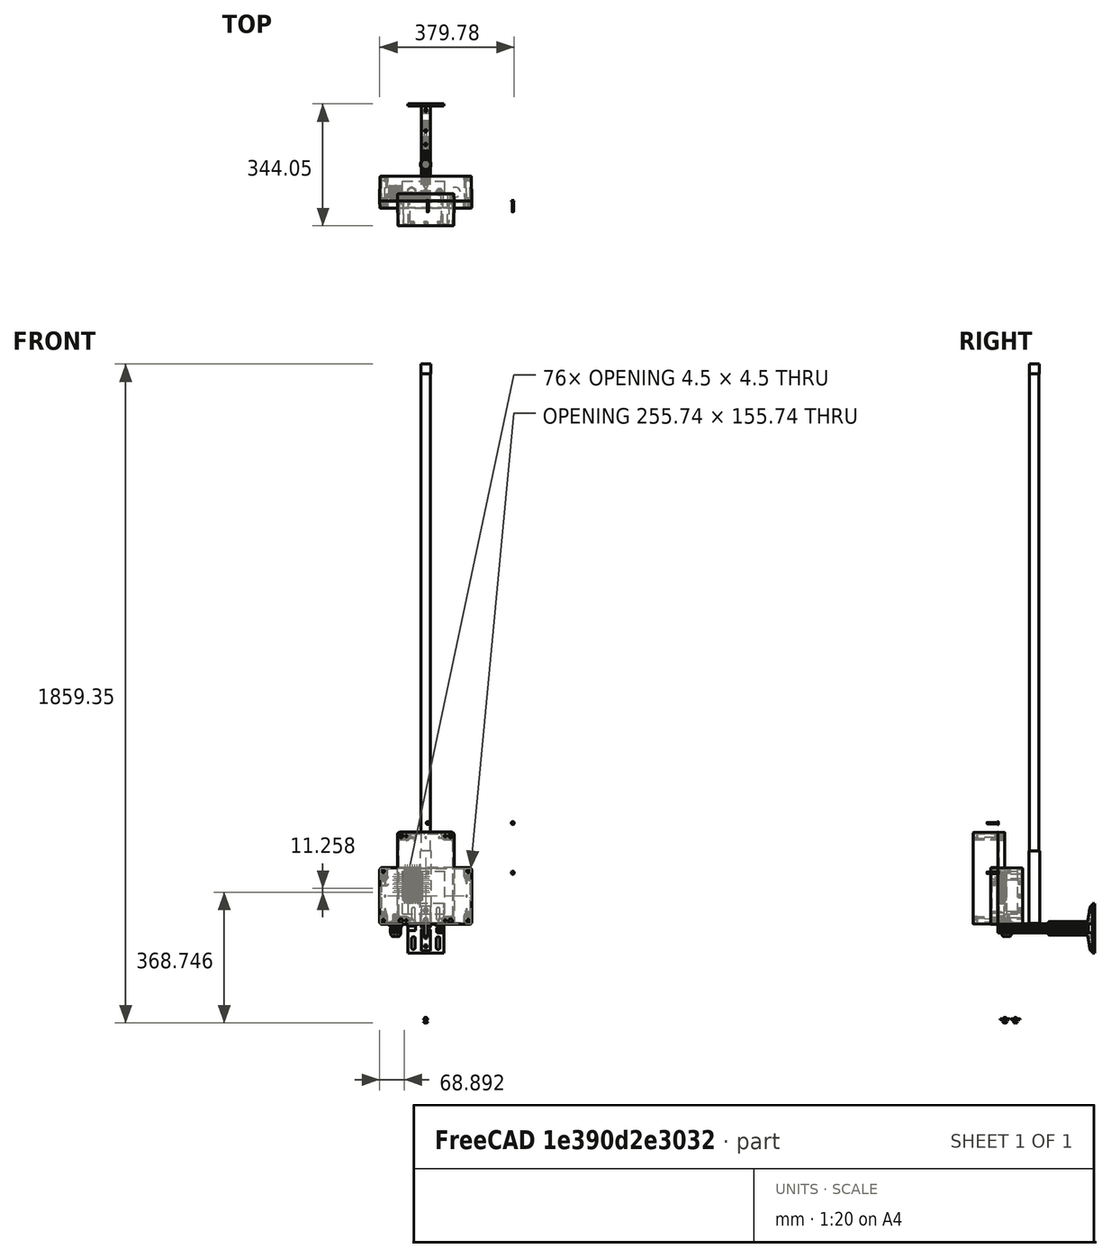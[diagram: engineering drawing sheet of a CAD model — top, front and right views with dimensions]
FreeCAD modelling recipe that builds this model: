
FCSTD DOCUMENT  (FreeCAD 0.20R29410 (Git))
Label: gateWayModule
License: All rights reserved
LicenseURL: http://en.wikipedia.org/wiki/All_rights_reserved
objects: Part::Feature×42, TechDraw::DrawViewDimension×36, Part::Cylinder×28, Part::MultiFuse×9, App::Part×8, Part::Cut×4, TechDraw::DrawViewPart×4, TechDraw::DrawSVGTemplate×2, TechDraw::DrawPage×2, Part::Box×1, Sketcher::SketchObject×1, Part::Extrusion×1, TechDraw::DrawViewAnnotation×1
note: 86 computed .brp shape members not serialized (recipe doc carries the construction recipe); baked Part::Feature solids carry a one-line shape summary decoded from their .brp

FEATURE [Part::Feature] Part__Feature  label="AN-23B_AN-23BP-01"
  shape: bbox 160 x 71.5 x 260 mm, 302 faces (baked)
FEATURE [Part::Feature] Part__Feature001  label="AN-23C_AN-23C-01"
  shape: bbox 160.5 x 20 x 260.5 mm, 243 faces (baked)
FEATURE [Part::Feature] Part__Feature002  label="cross recessed countersunk head screw_jis_JIS 1111 Cross recessed countersunk head screw - M4 x 32 - Z --24CSST"
  Placement = pos=(245.578,1.4369,155.7) rot=(0.642635,-0.642635,0.417181;3.93205rad)
  shape: bbox 8.4 x 32 x 8.4 mm, 32 faces (baked)
FEATURE [Part::Feature] Part__Feature003  label="cross recessed countersunk head screw_jis_JIS 1111 Cross recessed countersunk head screw - M4 x 32 - Z --24CSST001"
  Placement = pos=(245.578,1.4369,15.6996) rot=(0.610522,-0.610522,0.504506;4.07608rad)
  shape: bbox 8.4 x 32 x 8.4 mm, 32 faces (baked)
FEATURE [Part::Feature] Part__Feature004  label="cross recessed countersunk head screw_jis_JIS 1111 Cross recessed countersunk head screw - M4 x 32 - Z --24CSST002"
  Placement = pos=(5.5776,1.4369,15.6996) rot=(0.641113,-0.641113,0.421839;3.93997rad)
  shape: bbox 8.4 x 32 x 8.4 mm, 32 faces (baked)
FEATURE [Part::Feature] Part__Feature005  label="cross recessed countersunk head screw_jis_JIS 1111 Cross recessed countersunk head screw - M4 x 32 - Z --24CSST003"
  Placement = pos=(5.5776,1.4369,155.7) rot=(0.666667,-0.666667,0.333333;3.78509rad)
  shape: bbox 8.4 x 32 x 8.4 mm, 32 faces (baked)
FEATURE [App::Part] SCREWS_036_4  label="SCREWS-036-4"
  Group = -> [Part__Feature002,Part__Feature003,Part__Feature004,Part__Feature005]
  Origin = -> Origin
  Placement = pos=(85.6996,18.1356,-125.578) rot=(0,-1,0;1.5708rad)
FEATURE [Part::Feature] Part__Feature006  label="GASKET-123-01"
  Placement = pos=(0,1.04,0) rot=(0,0,1;0rad)
  shape: bbox 157.7 x 1.5 x 257.7 mm, 98 faces (baked)
FEATURE [App::Part] AN_23P_01  label="AN-23P-01"
  Group = -> [Part__Feature,Part__Feature001,SCREWS_036_4,Part__Feature006]
  Origin = -> Origin001
  Placement = pos=(0,0,-50) rot=(0.707107,0,-0.707107;3.14159rad)
FEATURE [Part::Box] Box  label="Gateway"
  AttacherType = Attacher::AttachEngine3D
  Height = 120
  Length = 120
  Placement = pos=(-66,26,-100) rot=(0,0,1;0rad)
  Width = 30
FEATURE [Part::Cylinder] Cylinder030  label="loraAntenna"
  Angle = 360
  AttacherType = Attacher::AttachEngine3D
  FirstAngle = 0
  Height = 1390
  Radius = 13
  SecondAngle = 0
FEATURE [Part::Cylinder] Cylinder031  label="loraAntenna001"
  Angle = 360
  AttacherType = Attacher::AttachEngine3D
  FirstAngle = 0
  Height = 204
  Radius = 15
  SecondAngle = 0
FEATURE [Part::Cylinder] Cylinder032  label="loraAntenna002"
  Angle = 360
  AttacherType = Attacher::AttachEngine3D
  FirstAngle = 0
  Height = 27
  Placement = pos=(0,0,1363) rot=(0,0,1;0rad)
  Radius = 14
  SecondAngle = 0
FEATURE [Part::MultiFuse] Fusion006  label="loraAntenna003"
  Placement = pos=(0,0,188) rot=(0,0,1;0rad)
  Shapes = -> [Cylinder030,Cylinder032]
FEATURE [Part::MultiFuse] Fusion007  label="loraAntenna004"
  Placement = pos=(0,103,-127) rot=(0,0,1;0rad)
  Shapes = -> [Fusion006,Cylinder031]
FEATURE [Part::Feature] Part__Feature008  label="CUI_VGS-25W-5"
  Placement = pos=(-42,23,-27) rot=(1,0,0;3.14159rad)
  shape: bbox 55.36 x 25.53 x 90.37 mm, 2734 faces, 26 solids (baked)
FEATURE [Part::Feature] Part__Feature009  label="DCC-RJ6ST-310"
  Placement = pos=(-85,25,-123) rot=(0,0,1;0rad)
  shape: bbox 40.36 x 68.07 x 51.72 mm, 441 faces (baked)
FEATURE [Part::Feature] Part__Feature010  label="DCP-RJ6ST-F"
  Placement = pos=(-85,25,-123.5) rot=(0,1,0;3.14159rad)
  shape: bbox 40.26 x 40.33 x 38.85 mm, 485 faces, 2 solids (baked)
FEATURE [Part::Cylinder] Cylinder  label="plugIn"
  Angle = 360
  AttacherType = Attacher::AttachEngine3D
  FirstAngle = 0
  Height = 28.19
  Radius = 11
  SecondAngle = 0
FEATURE [Sketcher::SketchObject] Sketch
  FullyConstrained = true
  sketch-geometry (7):
    g0: LineSegment StartX=12.25 StartY=-7.07254 StartZ=0 EndX=12.25 EndY=7.07254 EndZ=0
    g1: LineSegment StartX=12.25 StartY=7.07254 StartZ=0 EndX=0 EndY=14.1451 EndZ=0
    g2: LineSegment StartX=0 StartY=14.1451 StartZ=0 EndX=-12.25 EndY=7.07254 EndZ=0
    g3: LineSegment StartX=-12.25 StartY=7.07254 StartZ=0 EndX=-12.25 EndY=-7.07254 EndZ=0
    g4: LineSegment StartX=-12.25 StartY=-7.07254 StartZ=0 EndX=0 EndY=-14.1451 EndZ=0
    g5: LineSegment StartX=0 StartY=-14.1451 StartZ=0 EndX=12.25 EndY=-7.07254 EndZ=0
    g6: Circle CenterX=0 CenterY=0 CenterZ=0 NormalX=0 NormalY=0 NormalZ=1 AngleXU=0 Radius=14.1451
  constraints (17):
    c: Coincident(g0,g1)
    c: Coincident(g1,g2)
    c: Coincident(g2,g3)
    c: Coincident(g3,g4)
    c: Coincident(g4,g5)
    c: Coincident(g5,g0)
    c: Equal(g0, g1-g5) x5
    c: PointOnObject(g0,g6)
    c: PointOnObject(g1,g6)
    c: PointOnObject(g2,g6)
    c: PointOnObject(g3,g6)
    c: PointOnObject(g4,g6)
    c: PointOnObject(g5,g6)
    c: DistanceY(g6) = 0
    c: DistanceX(g6) = 0
    c: DistanceX(g1) = 0
    c: DistanceX(g2,g0) = 24.5
FEATURE [Part::Extrusion] Extrude
  Base = -> Sketch
  Dir = (0,0,1)
  DirMode = 2
  FaceMakerClass = Part::FaceMakerBullseye
  LengthFwd = 4.83
  LengthRev = 0
  Placement = pos=(0,0,12.19) rot=(0,0,1;0rad)
  Solid = true
  Symmetric = false
FEATURE [Part::MultiFuse] Fusion  label="powerPlug"
  Placement = pos=(-40,25,-147) rot=(0,0,1;0rad)
  Shapes = -> [Cylinder,Extrude]
FEATURE [Part::Feature] Part__Feature021  label="LoRaAntennaGland"
  Placement = pos=(84,25,-120) rot=(-1,0,0;1.5708rad)
  shape: bbox 36.99 x 36.69 x 48.04 mm, 518 faces, 0 solids (baked)
FEATURE [Part::Feature] Part__Feature022  label="3136N138_T-Slotted Framing"
  Placement = pos=(0,200.3,0) rot=(0,0,1;0rad)
  shape: bbox 101.6 x 133.4 x 139.7 mm, 136 faces (baked)
FEATURE [Part::Feature] Part__Feature023  label="47065T801_T-Slotted Framing"
  Placement = pos=(0,288.5,0) rot=(-1,0,0;1.5708rad)
  shape: bbox 25.4 x 152.4 x 25.4 mm, 108 faces (baked)
FEATURE [Part::Feature] Part__Feature024  label="47065T801_T-Slotted Framing001"
  Placement = pos=(0,391.5,0) rot=(-1,0,0;1.5708rad)
  shape: bbox 25.4 x 152.4 x 25.4 mm, 108 faces (baked)
FEATURE [Part::MultiFuse] Fusion008  label="framingSupport"
  Placement = pos=(0,468,-141.41) rot=(0,0,1;3.14159rad)
  Shapes = -> [Part__Feature024,Part__Feature022,Part__Feature023]
FEATURE [Part::Feature] Part__Feature025  label="Cable Gland PG7-PG19 Body_PG008"
  shape: bbox 17.67 x 27.9 x 16 mm, 147 faces (baked)
FEATURE [Part::Feature] Part__Feature026  label="Cable Gland PG7-PG19 Washer_PG008"
  Placement = pos=(0,-2.8,0) rot=(0,0,1;0rad)
  shape: bbox 16.6 x 1.2 x 16.6 mm, 6 faces (baked)
FEATURE [Part::Feature] Part__Feature027  label="Cable Gland PG7-PG19 Lock Nut_PG008"
  Placement = pos=(0,-5.6,0) rot=(0,0,1;3.14159rad)
  shape: bbox 19.6 x 5.77 x 19.6 mm, 32 faces (baked)
FEATURE [Part::Feature] Part__Feature028  label="Cable Gland PG7-PG19 Sleeve_PG008"
  Placement = pos=(0,13.65,0) rot=(0,0,1;0rad)
  shape: bbox 8.4 x 6.7 x 8.4 mm, 6 faces (baked)
FEATURE [Part::Feature] Part__Feature029  label="Cable Gland PG7-PG19 Gland Nut_PG008"
  Placement = pos=(0,10.95,0) rot=(0,-1,0;1.94172rad)
  shape: bbox 16.87 x 14 x 16.87 mm, 64 faces (baked)
FEATURE [Part::MultiFuse] Fusion011  label="pg7-Copper"
  Placement = pos=(39,25,-134) rot=(-1,0,0;1.5708rad)
  Shapes = -> [Part__Feature025,Part__Feature026,Part__Feature027,Part__Feature028,Part__Feature029]
FEATURE [Part::Cylinder] Cylinder033  label="EthernetCut"
  Angle = 360
  AttacherType = Attacher::AttachEngine3D
  FirstAngle = 0
  Height = 50
  Placement = pos=(-85,25,-147) rot=(0,0,1;0rad)
  Radius = 15.1
  SecondAngle = 0
FEATURE [Part::Cylinder] Cylinder034  label="PowerCut"
  Angle = 360
  AttacherType = Attacher::AttachEngine3D
  FirstAngle = 0
  Height = 50
  Placement = pos=(-40,25,-147) rot=(0,0,1;0rad)
  Radius = 11
  SecondAngle = 0
FEATURE [Part::Cylinder] Cylinder035  label="pg7Cut"
  Angle = 360
  AttacherType = Attacher::AttachEngine3D
  FirstAngle = 0
  Height = 50
  Placement = pos=(39,25,-147) rot=(0,0,1;0rad)
  Radius = 6.4
  SecondAngle = 0
FEATURE [Part::Cylinder] Cylinder036  label="AnetnnaCut"
  Angle = 360
  AttacherType = Attacher::AttachEngine3D
  FirstAngle = 0
  Height = 50
  Placement = pos=(84,25,-147) rot=(0,0,1;0rad)
  Radius = 14.2
  SecondAngle = 0
FEATURE [Part::Feature] Part__Feature030  label="47065T139_T-Slotted Framing"
  Placement = pos=(0,20,-405) rot=(0.57735,0.57735,-0.57735;4.18879rad)
  shape: bbox 11.25 x 25.4 x 17.44 mm, 56 faces, 2 solids (baked)
FEATURE [Part::Feature] Part__Feature031  label="47065T139_T-Slotted Framing001"
  Placement = pos=(0,50,-405) rot=(0.57735,0.57735,-0.57735;4.18879rad)
  shape: bbox 11.25 x 25.4 x 17.44 mm, 56 faces, 2 solids (baked)
FEATURE [Part::Cylinder] Cylinder037  label="m5Cut"
  Angle = 360
  AttacherType = Attacher::AttachEngine3D
  FirstAngle = 0
  Height = 50
  Placement = pos=(0,20,-147) rot=(0,0,1;0rad)
  Radius = 3.2
  SecondAngle = 0
FEATURE [Part::Cylinder] Cylinder038  label="m5Cut001"
  Angle = 360
  AttacherType = Attacher::AttachEngine3D
  FirstAngle = 0
  Height = 50
  Placement = pos=(0,50,-147) rot=(0,0,1;0rad)
  Radius = 3.2
  SecondAngle = 0
FEATURE [Part::MultiFuse] Fusion012
  Shapes = -> [Cylinder038,Cylinder037,Cylinder036,Cylinder035,Cylinder033,Cylinder034]
FEATURE [Part::Cut] Cut
  Base = -> AN_23P_01
  Tool = -> Fusion012
FEATURE [TechDraw::DrawSVGTemplate] Template
  EditableTexts = Designed_by_Name=Lakitha Wijeratne; Drawing_number=V1; FC-Date=November 14th 2022; FC-SC=0.5; FC-Title=MINTS Gateway Module; Subtitle=Cutouts for Polycase AN-23P Black
  Height = 210
  Orientation = 1
  Width = 297
FEATURE [TechDraw::DrawViewPart] View  label="Internal View"
  CoarseView = false
  Direction = (0.577,-0.577,0.577)
  Focus = 100
  HardHidden = false
  IsoCount = 0
  IsoHidden = false
  IsoVisible = false
  LockPosition = false
  Perspective = false
  Rotation = 0
  Scale = 0.5
  ScaleType = 0
  SeamHidden = false
  SeamVisible = true
  SmoothHidden = false
  SmoothVisible = true
  Source = -> [Cut]
  X = 221.274
  XDirection = (0.707,0.707,0)
  Y = 135.96
FEATURE [TechDraw::DrawViewPart] View001  label="Bottom View"
  CoarseView = false
  Direction = (0,0,-1)
  Focus = 100
  HardHidden = false
  IsoCount = 0
  IsoHidden = false
  IsoVisible = false
  LockPosition = false
  Perspective = false
  Rotation = 0
  Scale = 0.5
  ScaleType = 0
  SeamHidden = false
  SeamVisible = true
  SmoothHidden = false
  SmoothVisible = true
  Source = -> [Cut]
  X = 84.2092
  XDirection = (1,0,0)
  Y = 168.275
FEATURE [Part::Cylinder] Cylinder039  label="EthernetCut001"
  Angle = 360
  AttacherType = Attacher::AttachEngine3D
  FirstAngle = 0
  Height = 50
  Placement = pos=(-85,25,-147) rot=(0,0,1;0rad)
  Radius = 15.1
  SecondAngle = 0
FEATURE [Part::Cylinder] Cylinder040  label="PowerCut001"
  Angle = 360
  AttacherType = Attacher::AttachEngine3D
  FirstAngle = 0
  Height = 50
  Placement = pos=(-40,25,-147) rot=(0,0,1;0rad)
  Radius = 11
  SecondAngle = 0
FEATURE [Part::Cylinder] Cylinder041  label="pg7Cut001"
  Angle = 360
  AttacherType = Attacher::AttachEngine3D
  FirstAngle = 0
  Height = 50
  Placement = pos=(39,25,-147) rot=(0,0,1;0rad)
  Radius = 6.4
  SecondAngle = 0
FEATURE [Part::Cylinder] Cylinder042  label="AnetnnaCut001"
  Angle = 360
  AttacherType = Attacher::AttachEngine3D
  FirstAngle = 0
  Height = 50
  Placement = pos=(84,25,-147) rot=(0,0,1;0rad)
  Radius = 14.2
  SecondAngle = 0
FEATURE [Part::Cylinder] Cylinder043  label="m5Cut002"
  Angle = 360
  AttacherType = Attacher::AttachEngine3D
  FirstAngle = 0
  Height = 50
  Placement = pos=(0,20,-147) rot=(0,0,1;0rad)
  Radius = 3.2
  SecondAngle = 0
FEATURE [Part::Cylinder] Cylinder044  label="m5Cut003"
  Angle = 360
  AttacherType = Attacher::AttachEngine3D
  FirstAngle = 0
  Height = 50
  Placement = pos=(0,50,-147) rot=(0,0,1;0rad)
  Radius = 3.2
  SecondAngle = 0
FEATURE [Part::MultiFuse] Fusion013
  Shapes = -> [Cylinder044,Cylinder043,Cylinder042,Cylinder041,Cylinder039,Cylinder040]
FEATURE [Part::Feature] Part__Feature032  label="AN-23B_AN-23BP-002"
  shape: bbox 160 x 71.5 x 260 mm, 302 faces (baked)
FEATURE [Part::Feature] Part__Feature033  label="AN-23C_AN-23C-002"
  shape: bbox 160.5 x 20 x 260.5 mm, 243 faces (baked)
FEATURE [Part::Feature] Part__Feature034  label="cross recessed countersunk head screw_jis_JIS 1111 Cross recessed countersunk head screw - M4 x 32 - Z --24CSST004"
  Placement = pos=(245.578,1.4369,155.7) rot=(0.642635,-0.642635,0.417181;3.93205rad)
  shape: bbox 8.4 x 32 x 8.4 mm, 32 faces (baked)
FEATURE [Part::Feature] Part__Feature035  label="cross recessed countersunk head screw_jis_JIS 1111 Cross recessed countersunk head screw - M4 x 32 - Z --24CSST005"
  Placement = pos=(245.578,1.4369,15.6996) rot=(0.610522,-0.610522,0.504506;4.07608rad)
  shape: bbox 8.4 x 32 x 8.4 mm, 32 faces (baked)
FEATURE [Part::Feature] Part__Feature036  label="cross recessed countersunk head screw_jis_JIS 1111 Cross recessed countersunk head screw - M4 x 32 - Z --24CSST006"
  Placement = pos=(5.5776,1.4369,15.6996) rot=(0.641113,-0.641113,0.421839;3.93997rad)
  shape: bbox 8.4 x 32 x 8.4 mm, 32 faces (baked)
FEATURE [Part::Feature] Part__Feature037  label="cross recessed countersunk head screw_jis_JIS 1111 Cross recessed countersunk head screw - M4 x 32 - Z --24CSST007"
  Placement = pos=(5.5776,1.4369,155.7) rot=(0.666667,-0.666667,0.333333;3.78509rad)
  shape: bbox 8.4 x 32 x 8.4 mm, 32 faces (baked)
FEATURE [Part::Feature] Part__Feature038  label="GASKET-123-002"
  Placement = pos=(0,1.04,0) rot=(0,0,1;0rad)
  shape: bbox 157.7 x 1.5 x 257.7 mm, 98 faces (baked)
FEATURE [App::Part] SCREWS_036_005  label="SCREWS-036-005"
  Group = -> [Part__Feature034,Part__Feature035,Part__Feature036,Part__Feature037]
  Origin = -> Origin002
  Placement = pos=(85.6996,18.1356,-125.578) rot=(0,-1,0;1.5708rad)
FEATURE [App::Part] AN_23P_002  label="AN-23P-002"
  Group = -> [Part__Feature032,Part__Feature033,SCREWS_036_005,Part__Feature038]
  Origin = -> Origin003
  Placement = pos=(0,0,-50) rot=(0.707107,0,-0.707107;3.14159rad)
FEATURE [Part::Cut] Cut001  label="totalView"
  Base = -> AN_23P_002
  Tool = -> Fusion013
FEATURE [TechDraw::DrawViewPart] View002  label="External View"
  CoarseView = false
  Direction = (0.673,-0.641,-0.369)
  Focus = 100
  HardHidden = false
  IsoCount = 0
  IsoHidden = false
  IsoVisible = false
  LockPosition = false
  Perspective = false
  Rotation = 0
  Scale = 0.5
  ScaleType = 0
  SeamHidden = false
  SeamVisible = true
  SmoothHidden = false
  SmoothVisible = true
  Source = -> [Cut001]
  X = 86.3288
  XDirection = (0.739,0.594,0.316)
  Y = 76.7663
FEATURE [TechDraw::DrawViewDimension] Dimension
  AngleOverride = false
  Arbitrary = false
  ArbitraryTolerances = false
  EqualTolerance = true
  ExtensionAngle = 0
  FormatSpec = ⌀%.2w
  FormatSpecOverTolerance = %+.2w
  FormatSpecUnderTolerance = %+.2w
  Inverted = false
  LineAngle = 0
  LockPosition = false
  MeasureType = 1
  OverTolerance = 0
  References2D = -> [View001]
  Rotation = 0
  Scale = 0.5
  ScaleType = 0
  TheoreticalExact = false
  Type = 5
  UnderTolerance = 0
  X = -54.3759
  Y = 16.2133
FEATURE [TechDraw::DrawViewDimension] Dimension001
  AngleOverride = false
  Arbitrary = false
  ArbitraryTolerances = false
  EqualTolerance = true
  ExtensionAngle = 0
  FormatSpec = ⌀%.2w
  FormatSpecOverTolerance = %+.2w
  FormatSpecUnderTolerance = %+.2w
  Inverted = false
  LineAngle = 0
  LockPosition = false
  MeasureType = 1
  OverTolerance = 0
  References2D = -> [View001]
  Rotation = 0
  Scale = 0.5
  ScaleType = 0
  TheoreticalExact = false
  Type = 5
  UnderTolerance = 0
  X = -24.7872
  Y = 16.2975
FEATURE [TechDraw::DrawViewDimension] Dimension002
  AngleOverride = false
  Arbitrary = false
  ArbitraryTolerances = false
  EqualTolerance = true
  ExtensionAngle = 0
  FormatSpec = ⌀%.2w
  FormatSpecOverTolerance = %+.2w
  FormatSpecUnderTolerance = %+.2w
  Inverted = false
  LineAngle = 0
  LockPosition = false
  MeasureType = 1
  OverTolerance = 0
  References2D = -> [View001]
  Rotation = 0
  Scale = 0.5
  ScaleType = 0
  TheoreticalExact = false
  Type = 5
  UnderTolerance = 0
  X = 5.16691
  Y = 14.3503
FEATURE [TechDraw::DrawViewDimension] Dimension003
  AngleOverride = false
  Arbitrary = false
  ArbitraryTolerances = false
  EqualTolerance = true
  ExtensionAngle = 0
  FormatSpec = ⌀%.2w
  FormatSpecOverTolerance = %+.2w
  FormatSpecUnderTolerance = %+.2w
  Inverted = false
  LineAngle = 0
  LockPosition = false
  MeasureType = 1
  OverTolerance = 0
  References2D = -> [View001]
  Rotation = 0
  Scale = 0.5
  ScaleType = 0
  TheoreticalExact = false
  Type = 5
  UnderTolerance = 0
  X = 6.79278
  Y = 3.20489
FEATURE [TechDraw::DrawViewDimension] Dimension004
  AngleOverride = false
  Arbitrary = false
  ArbitraryTolerances = false
  EqualTolerance = true
  ExtensionAngle = 0
  FormatSpec = ⌀%.2w
  FormatSpecOverTolerance = %+.2w
  FormatSpecUnderTolerance = %+.2w
  Inverted = false
  LineAngle = 0
  LockPosition = false
  MeasureType = 1
  OverTolerance = 0
  References2D = -> [View001]
  Rotation = 0
  Scale = 0.5
  ScaleType = 0
  TheoreticalExact = false
  Type = 5
  UnderTolerance = 0
  X = 25.1396
  Y = 14.8713
FEATURE [TechDraw::DrawViewDimension] Dimension005
  AngleOverride = false
  Arbitrary = false
  ArbitraryTolerances = false
  EqualTolerance = true
  ExtensionAngle = 0
  FormatSpec = ⌀%.2w
  FormatSpecOverTolerance = %+.2w
  FormatSpecUnderTolerance = %+.2w
  Inverted = false
  LineAngle = 0
  LockPosition = false
  MeasureType = 1
  OverTolerance = 0
  References2D = -> [View001]
  Rotation = 0
  Scale = 0.5
  ScaleType = 0
  TheoreticalExact = false
  Type = 5
  UnderTolerance = 0
  X = 53.9059
  Y = 15.1805
FEATURE [TechDraw::DrawViewDimension] Dimension006
  AngleOverride = false
  Arbitrary = false
  ArbitraryTolerances = false
  EqualTolerance = true
  ExtensionAngle = 0
  FormatSpec = %.2w
  FormatSpecOverTolerance = %+.2w
  FormatSpecUnderTolerance = %+.2w
  Inverted = false
  LineAngle = 0
  LockPosition = false
  MeasureType = 1
  OverTolerance = 0
  References2D = -> [View001]
  Rotation = 0
  Scale = 0.5
  ScaleType = 0
  TheoreticalExact = false
  Type = 1
  UnderTolerance = 0
  X = -53.7744
  Y = -18.6501
FEATURE [TechDraw::DrawViewDimension] Dimension007
  AngleOverride = false
  Arbitrary = false
  ArbitraryTolerances = false
  EqualTolerance = true
  ExtensionAngle = 0
  FormatSpec = %.2w
  FormatSpecOverTolerance = %+.2w
  FormatSpecUnderTolerance = %+.2w
  Inverted = false
  LineAngle = 0
  LockPosition = false
  MeasureType = 1
  OverTolerance = 0
  References2D = -> [View001]
  Rotation = 0
  Scale = 0.5
  ScaleType = 0
  TheoreticalExact = false
  Type = 1
  UnderTolerance = 0
  X = -35.7058
  Y = -24.4298
FEATURE [TechDraw::DrawViewDimension] Dimension009
  AngleOverride = false
  Arbitrary = false
  ArbitraryTolerances = false
  EqualTolerance = true
  ExtensionAngle = 0
  FormatSpec = %.2w
  FormatSpecOverTolerance = %+.2w
  FormatSpecUnderTolerance = %+.2w
  Inverted = false
  LineAngle = 0
  LockPosition = false
  MeasureType = 1
  OverTolerance = 0
  References2D = -> [View001]
  Rotation = 0
  Scale = 0.5
  ScaleType = 0
  TheoreticalExact = false
  Type = 1
  UnderTolerance = 0
  X = -39.2827
  Y = -33.1748
FEATURE [TechDraw::DrawViewDimension] Dimension010
  AngleOverride = false
  Arbitrary = false
  ArbitraryTolerances = false
  EqualTolerance = true
  ExtensionAngle = 0
  FormatSpec = %.2w
  FormatSpecOverTolerance = %+.2w
  FormatSpecUnderTolerance = %+.2w
  Inverted = false
  LineAngle = 0
  LockPosition = false
  MeasureType = 1
  OverTolerance = 0
  References2D = -> [View001]
  Rotation = 0
  Scale = 0.5
  ScaleType = 0
  TheoreticalExact = false
  Type = 1
  UnderTolerance = 0
  X = 47.8554
  Y = -25.9182
FEATURE [TechDraw::DrawViewDimension] Dimension011
  AngleOverride = false
  Arbitrary = false
  ArbitraryTolerances = false
  EqualTolerance = true
  ExtensionAngle = 0
  FormatSpec = %.2w
  FormatSpecOverTolerance = %+.2w
  FormatSpecUnderTolerance = %+.2w
  Inverted = false
  LineAngle = 0
  LockPosition = false
  MeasureType = 1
  OverTolerance = 0
  References2D = -> [View001]
  Rotation = 0
  Scale = 0.5
  ScaleType = 0
  TheoreticalExact = false
  Type = 1
  UnderTolerance = 0
  X = 54.1367
  Y = -18.5094
FEATURE [TechDraw::DrawViewDimension] Dimension012
  AngleOverride = false
  Arbitrary = false
  ArbitraryTolerances = false
  EqualTolerance = true
  ExtensionAngle = 0
  FormatSpec = %.2w
  FormatSpecOverTolerance = %+.2w
  FormatSpecUnderTolerance = %+.2w
  Inverted = false
  LineAngle = 0
  LockPosition = false
  MeasureType = 1
  OverTolerance = 0
  References2D = -> [View001]
  Rotation = 0
  Scale = 0.5
  ScaleType = 0
  TheoreticalExact = false
  Type = 2
  UnderTolerance = 0
  X = -36.989
  Y = 15.3034
FEATURE [TechDraw::DrawViewDimension] Dimension013
  AngleOverride = false
  Arbitrary = false
  ArbitraryTolerances = false
  EqualTolerance = true
  ExtensionAngle = 0
  FormatSpec = %.2w
  FormatSpecOverTolerance = %+.2w
  FormatSpecUnderTolerance = %+.2w
  Inverted = false
  LineAngle = 0
  LockPosition = false
  MeasureType = 1
  OverTolerance = 0
  References2D = -> [View001]
  Rotation = 0
  Scale = 0.5
  ScaleType = 0
  TheoreticalExact = false
  Type = 1
  UnderTolerance = 0
  X = -29.3162
  Y = 29.8128
FEATURE [TechDraw::DrawViewDimension] Dimension014
  AngleOverride = false
  Arbitrary = false
  ArbitraryTolerances = false
  EqualTolerance = true
  ExtensionAngle = 0
  FormatSpec = %.2w
  FormatSpecOverTolerance = %+.2w
  FormatSpecUnderTolerance = %+.2w
  Inverted = false
  LineAngle = 0
  LockPosition = false
  MeasureType = 1
  OverTolerance = 0
  References2D = -> [View001]
  Rotation = 0
  Scale = 0.5
  ScaleType = 0
  TheoreticalExact = false
  Type = 2
  UnderTolerance = 0
  X = 14.9293
  Y = 13.6113
FEATURE [TechDraw::DrawViewDimension] Dimension015
  AngleOverride = false
  Arbitrary = false
  ArbitraryTolerances = false
  EqualTolerance = true
  ExtensionAngle = 0
  FormatSpec = %.2w
  FormatSpecOverTolerance = %+.2w
  FormatSpecUnderTolerance = %+.2w
  Inverted = false
  LineAngle = 0
  LockPosition = false
  MeasureType = 1
  OverTolerance = 0
  References2D = -> [View001]
  Rotation = 0
  Scale = 0.5
  ScaleType = 0
  TheoreticalExact = false
  Type = 2
  UnderTolerance = 0
  X = 34.9847
  Y = 13.4844
FEATURE [TechDraw::DrawViewAnnotation] Annotation
  Font = osifont
  LineSpace = 80
  LockPosition = false
  MaxWidth = -1
  Rotation = 0
  Scale = 0.5
  ScaleType = 0
  Text = MINTS Artwork
  TextSize = 5
  TextStyle = 0
  X = 74.9972
  Y = 88.0198
FEATURE [TechDraw::DrawViewDimension] Dimension016
  AngleOverride = false
  Arbitrary = false
  ArbitraryTolerances = false
  EqualTolerance = true
  ExtensionAngle = 0
  FormatSpec = %.2w
  FormatSpecOverTolerance = %+.2w
  FormatSpecUnderTolerance = %+.2w
  Inverted = false
  LineAngle = 0
  LockPosition = false
  MeasureType = 1
  OverTolerance = 0
  References2D = -> [View001]
  Rotation = 0
  Scale = 0.5
  ScaleType = 0
  TheoreticalExact = false
  Type = 2
  UnderTolerance = 0
  X = -4.81759
  Y = 14.1292
FEATURE [TechDraw::DrawViewDimension] Dimension017
  AngleOverride = false
  Arbitrary = false
  ArbitraryTolerances = false
  EqualTolerance = true
  ExtensionAngle = 0
  FormatSpec = %.2w
  FormatSpecOverTolerance = %+.2w
  FormatSpecUnderTolerance = %+.2w
  Inverted = false
  LineAngle = 0
  LockPosition = false
  MeasureType = 1
  OverTolerance = 0
  References2D = -> [View001]
  Rotation = 0
  Scale = 0.5
  ScaleType = 0
  TheoreticalExact = false
  Type = 2
  UnderTolerance = 0
  X = -10.0786
  Y = 5.19442
FEATURE [TechDraw::DrawViewDimension] Dimension018
  AngleOverride = false
  Arbitrary = false
  ArbitraryTolerances = false
  EqualTolerance = true
  ExtensionAngle = 0
  FormatSpec = %.2w
  FormatSpecOverTolerance = %+.2w
  FormatSpecUnderTolerance = %+.2w
  Inverted = false
  LineAngle = 0
  LockPosition = false
  MeasureType = 1
  OverTolerance = 0
  References2D = -> [View001]
  Rotation = 0
  Scale = 0.5
  ScaleType = 0
  TheoreticalExact = false
  Type = 2
  UnderTolerance = 0
  X = -16.9958
  Y = 14.4097
FEATURE [TechDraw::DrawPage] Page
  KeepUpdated = true
  NextBalloonIndex = 1
  ProjectionType = 0
  Scale = 0.5
  Template = -> Template
  Views = -> [View,View001,View002,Dimension,Dimension001,Dimension002,Dimension003,Dimension004,Dimension005,Dimension006,Dimension007,Dimension009,Dimension010,Dimension011,Dimension012,Dimension013,Dimension014,Dimension015,Annotation,Dimension016,Dimension017,Dimension018]
FEATURE [Part::Cylinder] Cylinder045  label="EthernetCut002"
  Angle = 360
  AttacherType = Attacher::AttachEngine3D
  FirstAngle = 0
  Height = 50
  Placement = pos=(-85,25,-147) rot=(0,0,1;0rad)
  Radius = 15.1
  SecondAngle = 0
FEATURE [Part::Cylinder] Cylinder046  label="PowerCut002"
  Angle = 360
  AttacherType = Attacher::AttachEngine3D
  FirstAngle = 0
  Height = 50
  Placement = pos=(-40,25,-147) rot=(0,0,1;0rad)
  Radius = 11
  SecondAngle = 0
FEATURE [Part::Cylinder] Cylinder047  label="pg7Cut002"
  Angle = 360
  AttacherType = Attacher::AttachEngine3D
  FirstAngle = 0
  Height = 50
  Placement = pos=(39,25,-147) rot=(0,0,1;0rad)
  Radius = 6.4
  SecondAngle = 0
FEATURE [Part::Cylinder] Cylinder048  label="AnetnnaCut002"
  Angle = 360
  AttacherType = Attacher::AttachEngine3D
  FirstAngle = 0
  Height = 50
  Placement = pos=(84,25,-147) rot=(0,0,1;0rad)
  Radius = 14.2
  SecondAngle = 0
FEATURE [Part::Cylinder] Cylinder049  label="m5Cut004"
  Angle = 360
  AttacherType = Attacher::AttachEngine3D
  FirstAngle = 0
  Height = 50
  Placement = pos=(0,20,-147) rot=(0,0,1;0rad)
  Radius = 3.2
  SecondAngle = 0
FEATURE [Part::Cylinder] Cylinder050  label="m5Cut005"
  Angle = 360
  AttacherType = Attacher::AttachEngine3D
  FirstAngle = 0
  Height = 50
  Placement = pos=(0,50,-147) rot=(0,0,1;0rad)
  Radius = 3.2
  SecondAngle = 0
FEATURE [Part::Cylinder] Cylinder051  label="EthernetCut003"
  Angle = 360
  AttacherType = Attacher::AttachEngine3D
  FirstAngle = 0
  Height = 50
  Placement = pos=(-85,25,-147) rot=(0,0,1;0rad)
  Radius = 15.1
  SecondAngle = 0
FEATURE [Part::Cylinder] Cylinder052  label="PowerCut003"
  Angle = 360
  AttacherType = Attacher::AttachEngine3D
  FirstAngle = 0
  Height = 50
  Placement = pos=(-40,25,-147) rot=(0,0,1;0rad)
  Radius = 11
  SecondAngle = 0
FEATURE [Part::Cylinder] Cylinder053  label="pg7Cut003"
  Angle = 360
  AttacherType = Attacher::AttachEngine3D
  FirstAngle = 0
  Height = 50
  Placement = pos=(39,25,-147) rot=(0,0,1;0rad)
  Radius = 6.4
  SecondAngle = 0
FEATURE [Part::Cylinder] Cylinder054  label="AnetnnaCut003"
  Angle = 360
  AttacherType = Attacher::AttachEngine3D
  FirstAngle = 0
  Height = 50
  Placement = pos=(84,25,-147) rot=(0,0,1;0rad)
  Radius = 14.2
  SecondAngle = 0
FEATURE [Part::Cylinder] Cylinder055  label="m5Cut006"
  Angle = 360
  AttacherType = Attacher::AttachEngine3D
  FirstAngle = 0
  Height = 50
  Placement = pos=(0,20,-147) rot=(0,0,1;0rad)
  Radius = 3.2
  SecondAngle = 0
FEATURE [Part::Cylinder] Cylinder056  label="m5Cut007"
  Angle = 360
  AttacherType = Attacher::AttachEngine3D
  FirstAngle = 0
  Height = 50
  Placement = pos=(0,50,-147) rot=(0,0,1;0rad)
  Radius = 3.2
  SecondAngle = 0
FEATURE [Part::MultiFuse] Fusion014
  Shapes = -> [Cylinder050,Cylinder049,Cylinder048,Cylinder047,Cylinder045,Cylinder046]
FEATURE [Part::MultiFuse] Fusion015
  Shapes = -> [Cylinder056,Cylinder055,Cylinder054,Cylinder053,Cylinder051,Cylinder052]
FEATURE [Part::Feature] Part__Feature039  label="AN-23B_AN-23BP-003"
  shape: bbox 160 x 71.5 x 260 mm, 302 faces (baked)
FEATURE [Part::Feature] Part__Feature040  label="AN-23C_AN-23C-003"
  shape: bbox 160.5 x 20 x 260.5 mm, 243 faces (baked)
FEATURE [Part::Feature] Part__Feature041  label="cross recessed countersunk head screw_jis_JIS 1111 Cross recessed countersunk head screw - M4 x 32 - Z --24CSST008"
  Placement = pos=(245.578,1.4369,155.7) rot=(0.642635,-0.642635,0.417181;3.93205rad)
  shape: bbox 8.4 x 32 x 8.4 mm, 32 faces (baked)
FEATURE [Part::Feature] Part__Feature042  label="cross recessed countersunk head screw_jis_JIS 1111 Cross recessed countersunk head screw - M4 x 32 - Z --24CSST009"
  Placement = pos=(245.578,1.4369,15.6996) rot=(0.610522,-0.610522,0.504506;4.07608rad)
  shape: bbox 8.4 x 32 x 8.4 mm, 32 faces (baked)
FEATURE [Part::Feature] Part__Feature043  label="cross recessed countersunk head screw_jis_JIS 1111 Cross recessed countersunk head screw - M4 x 32 - Z --24CSST010"
  Placement = pos=(5.5776,1.4369,15.6996) rot=(0.641113,-0.641113,0.421839;3.93997rad)
  shape: bbox 8.4 x 32 x 8.4 mm, 32 faces (baked)
FEATURE [Part::Feature] Part__Feature044  label="cross recessed countersunk head screw_jis_JIS 1111 Cross recessed countersunk head screw - M4 x 32 - Z --24CSST011"
  Placement = pos=(5.5776,1.4369,155.7) rot=(0.666667,-0.666667,0.333333;3.78509rad)
  shape: bbox 8.4 x 32 x 8.4 mm, 32 faces (baked)
FEATURE [Part::Feature] Part__Feature045  label="GASKET-123-003"
  Placement = pos=(0,1.04,0) rot=(0,0,1;0rad)
  shape: bbox 157.7 x 1.5 x 257.7 mm, 98 faces (baked)
FEATURE [Part::Feature] Part__Feature046  label="AN-23B_AN-23BP-004"
  shape: bbox 160 x 71.5 x 260 mm, 302 faces (baked)
FEATURE [Part::Feature] Part__Feature047  label="AN-23C_AN-23C-004"
  shape: bbox 160.5 x 20 x 260.5 mm, 243 faces (baked)
FEATURE [Part::Feature] Part__Feature048  label="cross recessed countersunk head screw_jis_JIS 1111 Cross recessed countersunk head screw - M4 x 32 - Z --24CSST012"
  Placement = pos=(245.578,1.4369,155.7) rot=(0.642635,-0.642635,0.417181;3.93205rad)
  shape: bbox 8.4 x 32 x 8.4 mm, 32 faces (baked)
FEATURE [Part::Feature] Part__Feature049  label="cross recessed countersunk head screw_jis_JIS 1111 Cross recessed countersunk head screw - M4 x 32 - Z --24CSST013"
  Placement = pos=(245.578,1.4369,15.6996) rot=(0.610522,-0.610522,0.504506;4.07608rad)
  shape: bbox 8.4 x 32 x 8.4 mm, 32 faces (baked)
FEATURE [Part::Feature] Part__Feature050  label="cross recessed countersunk head screw_jis_JIS 1111 Cross recessed countersunk head screw - M4 x 32 - Z --24CSST014"
  Placement = pos=(5.5776,1.4369,15.6996) rot=(0.641113,-0.641113,0.421839;3.93997rad)
  shape: bbox 8.4 x 32 x 8.4 mm, 32 faces (baked)
FEATURE [Part::Feature] Part__Feature051  label="cross recessed countersunk head screw_jis_JIS 1111 Cross recessed countersunk head screw - M4 x 32 - Z --24CSST015"
  Placement = pos=(5.5776,1.4369,155.7) rot=(0.666667,-0.666667,0.333333;3.78509rad)
  shape: bbox 8.4 x 32 x 8.4 mm, 32 faces (baked)
FEATURE [Part::Feature] Part__Feature052  label="GASKET-123-004"
  Placement = pos=(0,1.04,0) rot=(0,0,1;0rad)
  shape: bbox 157.7 x 1.5 x 257.7 mm, 98 faces (baked)
FEATURE [App::Part] SCREWS_036_006  label="SCREWS-036-006"
  Group = -> [Part__Feature048,Part__Feature049,Part__Feature050,Part__Feature051]
  Origin = -> Origin006
  Placement = pos=(85.6996,18.1356,-125.578) rot=(0,-1,0;1.5708rad)
FEATURE [App::Part] AN_23P_003  label="AN-23P-003"
  Group = -> [Part__Feature046,Part__Feature047,SCREWS_036_006,Part__Feature052]
  Origin = -> Origin007
  Placement = pos=(0,0,-50) rot=(0.707107,0,-0.707107;3.14159rad)
FEATURE [Part::Cut] Cut003  label="totalView001"
  Base = -> AN_23P_003
  Tool = -> Fusion015
FEATURE [App::Part] SCREWS_036_007  label="SCREWS-036-007"
  Group = -> [Part__Feature041,Part__Feature042,Part__Feature043,Part__Feature044]
  Origin = -> Origin004
  Placement = pos=(85.6996,18.1356,-125.578) rot=(0,-1,0;1.5708rad)
FEATURE [App::Part] AN_23P_004  label="AN-23P-004"
  Group = -> [Part__Feature039,Part__Feature040,SCREWS_036_007,Part__Feature045]
  Origin = -> Origin005
  Placement = pos=(0,0,-50) rot=(0.707107,0,-0.707107;3.14159rad)
FEATURE [Part::Cut] Cut002
  Base = -> AN_23P_004
  Tool = -> Fusion014
FEATURE [TechDraw::DrawSVGTemplate] Template001
  EditableTexts = Designed_by_Name=Lakitha Wijeratne; Drawing_number=V1 - Bottom View; FC-Date=November 14th 2022; FC-SC=0.5; FC-Title=MINTS Gateway Module; Subtitle=Cutouts for Polycase AN-23P Black
  Height = 210
  Orientation = 1
  Width = 297
FEATURE [TechDraw::DrawViewPart] View004  label="Bottom View (Only)"
  CoarseView = false
  Direction = (0,0,-1)
  Focus = 100
  HardHidden = false
  IsoCount = 0
  IsoHidden = false
  IsoVisible = false
  LockPosition = false
  Perspective = false
  Rotation = 0
  ScaleType = 0
  SeamHidden = false
  SeamVisible = true
  SmoothHidden = false
  SmoothVisible = true
  Source = -> [Cut002]
  X = 148.914
  XDirection = (1,0,0)
  Y = 126.658
FEATURE [TechDraw::DrawViewDimension] Dimension019
  AngleOverride = false
  Arbitrary = false
  ArbitraryTolerances = false
  EqualTolerance = true
  ExtensionAngle = 0
  FormatSpec = ⌀%.2w
  FormatSpecOverTolerance = %+.2w
  FormatSpecUnderTolerance = %+.2w
  Inverted = false
  LineAngle = 0
  LockPosition = false
  MeasureType = 1
  OverTolerance = 0
  References2D = -> [View004]
  Rotation = 0
  ScaleType = 0
  TheoreticalExact = false
  Type = 5
  UnderTolerance = 0
  X = -79.9713
  Y = 18.1822
FEATURE [TechDraw::DrawViewDimension] Dimension020
  AngleOverride = false
  Arbitrary = false
  ArbitraryTolerances = false
  EqualTolerance = true
  ExtensionAngle = 0
  FormatSpec = ⌀%.2w
  FormatSpecOverTolerance = %+.2w
  FormatSpecUnderTolerance = %+.2w
  Inverted = false
  LineAngle = 0
  LockPosition = false
  MeasureType = 1
  OverTolerance = 0
  References2D = -> [View004]
  Rotation = 0
  ScaleType = 0
  TheoreticalExact = false
  Type = 5
  UnderTolerance = 0
  X = -35.8621
  Y = 16.7897
FEATURE [TechDraw::DrawViewDimension] Dimension021
  AngleOverride = false
  Arbitrary = false
  ArbitraryTolerances = false
  EqualTolerance = true
  ExtensionAngle = 0
  FormatSpec = ⌀%.2w
  FormatSpecOverTolerance = %+.2w
  FormatSpecUnderTolerance = %+.2w
  Inverted = false
  LineAngle = 0
  LockPosition = false
  MeasureType = 1
  OverTolerance = 0
  References2D = -> [View004]
  Rotation = 0
  ScaleType = 0
  TheoreticalExact = false
  Type = 5
  UnderTolerance = 0
  X = 5.16691
  Y = 28.6246
FEATURE [TechDraw::DrawViewDimension] Dimension022
  AngleOverride = false
  Arbitrary = false
  ArbitraryTolerances = false
  EqualTolerance = true
  ExtensionAngle = 0
  FormatSpec = ⌀%.2w
  FormatSpecOverTolerance = %+.2w
  FormatSpecUnderTolerance = %+.2w
  Inverted = false
  LineAngle = 0
  LockPosition = false
  MeasureType = 1
  OverTolerance = 0
  References2D = -> [View004]
  Rotation = 0
  ScaleType = 0
  TheoreticalExact = false
  Type = 5
  UnderTolerance = 0
  X = 7.77722
  Y = -3.93228
FEATURE [TechDraw::DrawViewDimension] Dimension023
  AngleOverride = false
  Arbitrary = false
  ArbitraryTolerances = false
  EqualTolerance = true
  ExtensionAngle = 0
  FormatSpec = ⌀%.2w
  FormatSpecOverTolerance = %+.2w
  FormatSpecUnderTolerance = %+.2w
  Inverted = false
  LineAngle = 0
  LockPosition = false
  MeasureType = 1
  OverTolerance = 0
  References2D = -> [View004]
  Rotation = 0
  ScaleType = 0
  TheoreticalExact = false
  Type = 5
  UnderTolerance = 0
  X = 52.95
  Y = 26.1923
FEATURE [TechDraw::DrawViewDimension] Dimension024
  AngleOverride = false
  Arbitrary = false
  ArbitraryTolerances = false
  EqualTolerance = true
  ExtensionAngle = 0
  FormatSpec = ⌀%.2w
  FormatSpecOverTolerance = %+.2w
  FormatSpecUnderTolerance = %+.2w
  Inverted = false
  LineAngle = 0
  LockPosition = false
  MeasureType = 1
  OverTolerance = 0
  References2D = -> [View004]
  Rotation = 0
  ScaleType = 0
  TheoreticalExact = false
  Type = 5
  UnderTolerance = 0
  X = 89.0995
  Y = 16.9032
FEATURE [TechDraw::DrawViewDimension] Dimension025
  AngleOverride = false
  Arbitrary = false
  ArbitraryTolerances = false
  EqualTolerance = true
  ExtensionAngle = 0
  FormatSpec = %.2w
  FormatSpecOverTolerance = %+.2w
  FormatSpecUnderTolerance = %+.2w
  Inverted = false
  LineAngle = 0
  LockPosition = false
  MeasureType = 1
  OverTolerance = 0
  References2D = -> [View004]
  Rotation = 0
  ScaleType = 0
  TheoreticalExact = false
  Type = 1
  UnderTolerance = 0
  X = -104.965
  Y = -7.57519
FEATURE [TechDraw::DrawViewDimension] Dimension026
  AngleOverride = false
  Arbitrary = false
  ArbitraryTolerances = false
  EqualTolerance = true
  ExtensionAngle = 0
  FormatSpec = %.2w
  FormatSpecOverTolerance = %+.2w
  FormatSpecUnderTolerance = %+.2w
  Inverted = false
  LineAngle = 0
  LockPosition = false
  MeasureType = 1
  OverTolerance = 0
  References2D = -> [View004]
  Rotation = 0
  ScaleType = 0
  TheoreticalExact = false
  Type = 1
  UnderTolerance = 0
  X = -63.7623
  Y = -9.66322
FEATURE [TechDraw::DrawViewDimension] Dimension027
  AngleOverride = false
  Arbitrary = false
  ArbitraryTolerances = false
  EqualTolerance = true
  ExtensionAngle = 0
  FormatSpec = %.2w
  FormatSpecOverTolerance = %+.2w
  FormatSpecUnderTolerance = %+.2w
  Inverted = false
  LineAngle = 0
  LockPosition = false
  MeasureType = 1
  OverTolerance = 0
  References2D = -> [View004]
  Rotation = 0
  ScaleType = 0
  TheoreticalExact = false
  Type = 1
  UnderTolerance = 0
  X = -63.6475
  Y = -23.3304
FEATURE [TechDraw::DrawViewDimension] Dimension028
  AngleOverride = false
  Arbitrary = false
  ArbitraryTolerances = false
  EqualTolerance = true
  ExtensionAngle = 0
  FormatSpec = %.2w
  FormatSpecOverTolerance = %+.2w
  FormatSpecUnderTolerance = %+.2w
  Inverted = false
  LineAngle = 0
  LockPosition = false
  MeasureType = 1
  OverTolerance = 0
  References2D = -> [View004]
  Rotation = 0
  ScaleType = 0
  TheoreticalExact = false
  Type = 1
  UnderTolerance = 0
  X = 98.0616
  Y = -20.7499
FEATURE [TechDraw::DrawViewDimension] Dimension029
  AngleOverride = false
  Arbitrary = false
  ArbitraryTolerances = false
  EqualTolerance = true
  ExtensionAngle = 0
  FormatSpec = %.2w
  FormatSpecOverTolerance = %+.2w
  FormatSpecUnderTolerance = %+.2w
  Inverted = false
  LineAngle = 0
  LockPosition = false
  MeasureType = 1
  OverTolerance = 0
  References2D = -> [View004]
  Rotation = 0
  ScaleType = 0
  TheoreticalExact = false
  Type = 1
  UnderTolerance = 0
  X = 106.312
  Y = -8.66499
FEATURE [TechDraw::DrawViewDimension] Dimension030
  AngleOverride = false
  Arbitrary = false
  ArbitraryTolerances = false
  EqualTolerance = true
  ExtensionAngle = 0
  FormatSpec = %.2w
  FormatSpecOverTolerance = %+.2w
  FormatSpecUnderTolerance = %+.2w
  Inverted = false
  LineAngle = 0
  LockPosition = false
  MeasureType = 1
  OverTolerance = 0
  References2D = -> [View004]
  Rotation = 0
  ScaleType = 0
  TheoreticalExact = false
  Type = 2
  UnderTolerance = 0
  X = -110.822
  Y = 26.8705
FEATURE [TechDraw::DrawViewDimension] Dimension031
  AngleOverride = false
  Arbitrary = false
  ArbitraryTolerances = false
  EqualTolerance = true
  ExtensionAngle = 0
  FormatSpec = %.2w
  FormatSpecOverTolerance = %+.2w
  FormatSpecUnderTolerance = %+.2w
  Inverted = false
  LineAngle = 0
  LockPosition = false
  MeasureType = 1
  OverTolerance = 0
  References2D = -> [View004]
  Rotation = 0
  ScaleType = 0
  TheoreticalExact = false
  Type = 1
  UnderTolerance = 0
  X = -68.4476
  Y = 54.6698
FEATURE [TechDraw::DrawViewDimension] Dimension032
  AngleOverride = false
  Arbitrary = false
  ArbitraryTolerances = false
  EqualTolerance = true
  ExtensionAngle = 0
  FormatSpec = %.2w
  FormatSpecOverTolerance = %+.2w
  FormatSpecUnderTolerance = %+.2w
  Inverted = false
  LineAngle = 0
  LockPosition = false
  MeasureType = 1
  OverTolerance = 0
  References2D = -> [View004]
  Rotation = 0
  ScaleType = 0
  TheoreticalExact = false
  Type = 2
  UnderTolerance = 0
  X = 15.4215
  Y = 20.9946
FEATURE [TechDraw::DrawViewDimension] Dimension033
  AngleOverride = false
  Arbitrary = false
  ArbitraryTolerances = false
  EqualTolerance = true
  ExtensionAngle = 0
  FormatSpec = %.2w
  FormatSpecOverTolerance = %+.2w
  FormatSpecUnderTolerance = %+.2w
  Inverted = false
  LineAngle = 0
  LockPosition = false
  MeasureType = 1
  OverTolerance = 0
  References2D = -> [View004]
  Rotation = 0
  ScaleType = 0
  TheoreticalExact = false
  Type = 2
  UnderTolerance = 0
  X = 27.3553
  Y = 23.3288
FEATURE [TechDraw::DrawViewDimension] Dimension034
  AngleOverride = false
  Arbitrary = false
  ArbitraryTolerances = false
  EqualTolerance = true
  ExtensionAngle = 0
  FormatSpec = %.2w
  FormatSpecOverTolerance = %+.2w
  FormatSpecUnderTolerance = %+.2w
  Inverted = false
  LineAngle = 0
  LockPosition = false
  MeasureType = 1
  OverTolerance = 0
  References2D = -> [View004]
  Rotation = 0
  ScaleType = 0
  TheoreticalExact = false
  Type = 2
  UnderTolerance = 0
  X = -9.24755
  Y = 25.9425
FEATURE [TechDraw::DrawViewDimension] Dimension035
  AngleOverride = false
  Arbitrary = false
  ArbitraryTolerances = false
  EqualTolerance = true
  ExtensionAngle = 0
  FormatSpec = %.2w
  FormatSpecOverTolerance = %+.2w
  FormatSpecUnderTolerance = %+.2w
  Inverted = false
  LineAngle = 0
  LockPosition = false
  MeasureType = 1
  OverTolerance = 0
  References2D = -> [View004]
  Rotation = 0
  ScaleType = 0
  TheoreticalExact = false
  Type = 2
  UnderTolerance = 0
  X = -18.9385
  Y = 1.74889
FEATURE [TechDraw::DrawViewDimension] Dimension036
  AngleOverride = false
  Arbitrary = false
  ArbitraryTolerances = false
  EqualTolerance = true
  ExtensionAngle = 0
  FormatSpec = %.2w
  FormatSpecOverTolerance = %+.2w
  FormatSpecUnderTolerance = %+.2w
  Inverted = false
  LineAngle = 0
  LockPosition = false
  MeasureType = 1
  OverTolerance = 0
  References2D = -> [View004]
  Rotation = 0
  ScaleType = 0
  TheoreticalExact = false
  Type = 2
  UnderTolerance = 0
  X = -57.8499
  Y = 23.7618
FEATURE [TechDraw::DrawPage] Page001
  KeepUpdated = true
  NextBalloonIndex = 1
  ProjectionType = 0
  Template = -> Template001
  Views = -> [View004,Dimension019,Dimension020,Dimension021,Dimension022,Dimension023,Dimension024,Dimension025,Dimension026,Dimension027,Dimension028,Dimension029,Dimension030,Dimension031,Dimension032,Dimension033,Dimension034,Dimension035,Dimension036]
